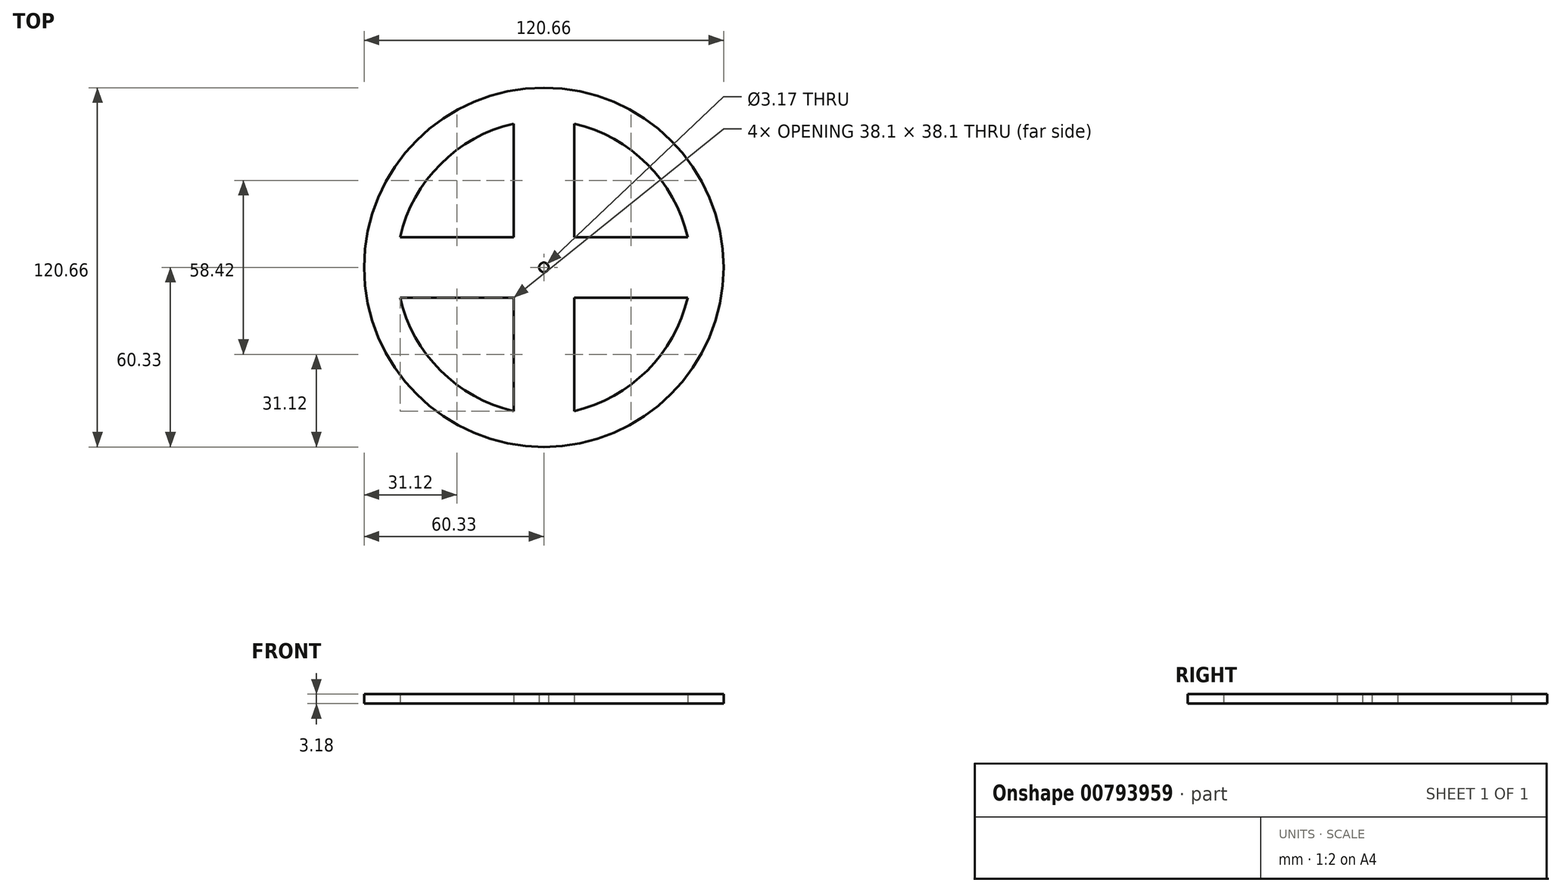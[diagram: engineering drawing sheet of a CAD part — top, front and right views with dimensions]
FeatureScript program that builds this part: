
annotation { "Feature Type Name" : "Feature", "Feature Type Description" : "" }
export const myFeature = defineFeature(function(context is Context, id is Id, definition is map)
    precondition{}
    {
        {
            var Q0;
            Q0=qCreatedBy(makeId("Top.planeOp"),FACE);
            var sketch = newSketch(context, id + "F0", { "sketchPlane" : qUnion([Q0])});
            skCircle(sketch, "E0", {"center": v(0, 0) * mm, "radius": 60.33 * mm});
            skLineSegment(sketch, "E1", {"start": v(0, 60.33) * mm, "end": v(0, 0) * mm});
            skLineSegment(sketch, "E2", {"start": v(60.33, 0) * mm, "end": v(0, 0) * mm});
            skLineSegment(sketch, "E3", {"start": v(0, -60.33) * mm, "end": v(0, 0) * mm});
            skLineSegment(sketch, "E4", {"start": v(-60.33, 0) * mm, "end": v(0, 0) * mm});
            skLineSegment(sketch, "E5", {"start": v(0, 0) * mm, "end": v(-42.66, 42.66) * mm});
            skLineSegment(sketch, "E6", {"start": v(0, 0) * mm, "end": v(42.66, 42.66) * mm});
            skLineSegment(sketch, "E7", {"start": v(0, 0) * mm, "end": v(42.66, -42.66) * mm});
            skLineSegment(sketch, "E8", {"start": v(0, 0) * mm, "end": v(-42.66, -42.66) * mm});
            skCircle(sketch, "E9", {"center": v(0, 0) * mm, "radius": 17.78 * mm});
            skLineSegment(sketch, "E10", {"start": v(0, 0) * mm, "end": v(0, 48.26) * mm});
            skLineSegment(sketch, "E11", {"start": v(0, 0) * mm, "end": v(48.26, 0) * mm});
            skLineSegment(sketch, "E12", {"start": v(0, 0) * mm, "end": v(-48.26, 0) * mm});
            skLineSegment(sketch, "E13", {"start": v(0, 0) * mm, "end": v(0, -48.26) * mm});
            skLineSegment(sketch, "E14", {"start": v(-48.26, 0) * mm, "end": v(-48.26, 10.16) * mm});
            skLineSegment(sketch, "E15", {"start": v(-48.26, 0) * mm, "end": v(-48.26, -10.16) * mm});
            skLineSegment(sketch, "E16", {"start": v(0, 48.26) * mm, "end": v(10.16, 48.26) * mm});
            skLineSegment(sketch, "E17", {"start": v(0, 48.26) * mm, "end": v(-10.16, 48.26) * mm});
            skLineSegment(sketch, "E18", {"start": v(48.26, 0) * mm, "end": v(48.26, -10.16) * mm});
            skLineSegment(sketch, "E19", {"start": v(48.26, 0) * mm, "end": v(48.26, 10.16) * mm});
            skLineSegment(sketch, "E20", {"start": v(0, -48.26) * mm, "end": v(10.16, -48.26) * mm});
            skLineSegment(sketch, "E21", {"start": v(0, -48.26) * mm, "end": v(-10.16, -48.26) * mm});
            skLineSegment(sketch, "E22.bottom", {"start": v(0, 0) * mm, "end": v(-10.16, 0) * mm});
            skLineSegment(sketch, "E22.top", {"start": v(0, 10.16) * mm, "end": v(-10.16, 10.16) * mm});
            skLineSegment(sketch, "E22.left", {"start": v(0, 0) * mm, "end": v(0, 10.16) * mm});
            skLineSegment(sketch, "E22.right", {"start": v(-10.16, 0) * mm, "end": v(-10.16, 10.16) * mm});
            skPoint(sketch, "E23.oppositeSnap0", {"position": v(-5.08, 10.16) * mm});
            skLineSegment(sketch, "E23.bottom", {"start": v(0, 0) * mm, "end": v(10.16, 0) * mm});
            skLineSegment(sketch, "E23.top", {"start": v(0, 10.16) * mm, "end": v(10.16, 10.16) * mm});
            skLineSegment(sketch, "E23.right", {"start": v(10.16, 0) * mm, "end": v(10.16, 10.16) * mm});
            skLineSegment(sketch, "E24.top", {"start": v(0, -10.16) * mm, "end": v(10.16, -10.16) * mm});
            skLineSegment(sketch, "E24.left", {"start": v(0, 0) * mm, "end": v(0, -10.16) * mm});
            skLineSegment(sketch, "E24.right", {"start": v(10.16, 0) * mm, "end": v(10.16, -10.16) * mm});
            skLineSegment(sketch, "E25.top", {"start": v(0, -10.16) * mm, "end": v(-10.16, -10.16) * mm});
            skLineSegment(sketch, "E25.right", {"start": v(-10.16, 0) * mm, "end": v(-10.16, -10.16) * mm});
            skLineSegment(sketch, "E26", {"start": v(-10.16, 48.26) * mm, "end": v(-10.16, 10.16) * mm});
            skLineSegment(sketch, "E27", {"start": v(-48.26, 10.16) * mm, "end": v(-10.16, 10.16) * mm});
            skLineSegment(sketch, "E28", {"start": v(10.16, 48.26) * mm, "end": v(10.16, 10.16) * mm});
            skLineSegment(sketch, "E29", {"start": v(48.26, 10.16) * mm, "end": v(10.16, 10.16) * mm});
            skLineSegment(sketch, "E30", {"start": v(-48.26, -10.16) * mm, "end": v(-10.16, -10.16) * mm});
            skLineSegment(sketch, "E31", {"start": v(-10.16, -10.16) * mm, "end": v(-10.16, -48.26) * mm});
            skLineSegment(sketch, "E32", {"start": v(10.16, -48.26) * mm, "end": v(10.16, -10.16) * mm});
            skLineSegment(sketch, "E33", {"start": v(48.26, -10.16) * mm, "end": v(10.16, -10.16) * mm});
            skArc(sketch, "E34", {"start": v(-10.16, 48.26) * mm, "mid": v(-34.68, 34.68) * mm, "end": v(-48.26, 10.16) * mm});
            skArc(sketch, "E35", {"start": v(48.26, 10.16) * mm, "mid": v(34.68, 34.68) * mm, "end": v(10.16, 48.26) * mm});
            skArc(sketch, "E36", {"start": v(-48.26, -10.16) * mm, "mid": v(-34.68, -34.68) * mm, "end": v(-10.16, -48.26) * mm});
            skArc(sketch, "E37", {"start": v(10.16, -48.26) * mm, "mid": v(34.68, -34.68) * mm, "end": v(48.26, -10.16) * mm});
            skCircle(sketch, "E38", {"center": v(0, 0) * mm, "radius": 1.59 * mm});
            skSolve(sketch);
        }
        {
            var Q0;
            {var subQ5=sQuery(id+"F0.wireOp",EDGE,"E16");Q0=makeQuery(id+"F0.imprint","IMPRINT",FACE,{"disambiguationData":[TD([[makeQuery(id+"F0.imprint","IMPRINT",EDGE,{"derivedFrom":subQ5}),1.0]])]});}
            var Q1;
            {var subQ0=sQuery(id+"F0.wireOp",EDGE,"E19");Q1=makeQuery(id+"F0.imprint","IMPRINT",FACE,{"disambiguationData":[TD([[makeQuery(id+"F0.imprint","IMPRINT",EDGE,{"derivedFrom":subQ0}),-1.0]])]});}
            var Q2;
            {var subQ5=sQuery(id+"F0.wireOp",EDGE,"E17");Q2=makeQuery(id+"F0.imprint","IMPRINT",FACE,{"disambiguationData":[TD([[makeQuery(id+"F0.imprint","IMPRINT",EDGE,{"derivedFrom":subQ5}),-1.0]])]});}
            var Q3;
            {var subQ5=sQuery(id+"F0.wireOp",EDGE,"E14");Q3=makeQuery(id+"F0.imprint","IMPRINT",FACE,{"disambiguationData":[TD([[makeQuery(id+"F0.imprint","IMPRINT",EDGE,{"derivedFrom":subQ5}),1.0]])]});}
            var Q4;
            {var subQ0=sQuery(id+"F0.wireOp",EDGE,"E17");Q4=makeQuery(id+"F0.imprint","IMPRINT",FACE,{"disambiguationData":[TD([[makeQuery(id+"F0.imprint","IMPRINT",EDGE,{"derivedFrom":subQ0}),1.0]])]});}
            var Q5;
            {var subQ0=sQuery(id+"F0.wireOp",EDGE,"E16");Q5=makeQuery(id+"F0.imprint","IMPRINT",FACE,{"disambiguationData":[TD([[makeQuery(id+"F0.imprint","IMPRINT",EDGE,{"derivedFrom":subQ0}),-1.0]])]});}
            var Q6;
            {var subQ0=sQuery(id+"F0.wireOp",EDGE,"E23.top");Q6=makeQuery(id+"F0.imprint","IMPRINT",FACE,{"disambiguationData":[TD([[makeQuery(id+"F0.imprint","IMPRINT",EDGE,{"derivedFrom":subQ0}),1.0]])]});}
            var Q7;
            {var subQ0=sQuery(id+"F0.wireOp",EDGE,"E22.top");Q7=makeQuery(id+"F0.imprint","IMPRINT",FACE,{"disambiguationData":[TD([[makeQuery(id+"F0.imprint","IMPRINT",EDGE,{"derivedFrom":subQ0}),-1.0]])]});}
            var Q8;
            {var subQ0=sQuery(id+"F0.wireOp",EDGE,"E22.top");Q8=makeQuery(id+"F0.imprint","IMPRINT",FACE,{"disambiguationData":[TD([[makeQuery(id+"F0.imprint","IMPRINT",EDGE,{"derivedFrom":subQ0}),1.0]])]});}
            var Q9;
            {var subQ0=sQuery(id+"F0.wireOp",EDGE,"E22.right");Q9=makeQuery(id+"F0.imprint","IMPRINT",FACE,{"disambiguationData":[TD([[makeQuery(id+"F0.imprint","IMPRINT",EDGE,{"derivedFrom":subQ0}),-1.0]])]});}
            var Q10;
            {var subQ0=sQuery(id+"F0.wireOp",EDGE,"E22.right");Q10=makeQuery(id+"F0.imprint","IMPRINT",FACE,{"disambiguationData":[TD([[makeQuery(id+"F0.imprint","IMPRINT",EDGE,{"derivedFrom":subQ0}),1.0]])]});}
            var Q11;
            {var subQ0=sQuery(id+"F0.wireOp",EDGE,"E23.right");Q11=makeQuery(id+"F0.imprint","IMPRINT",FACE,{"disambiguationData":[TD([[makeQuery(id+"F0.imprint","IMPRINT",EDGE,{"derivedFrom":subQ0}),-1.0]])]});}
            var Q12;
            {var subQ0=sQuery(id+"F0.wireOp",EDGE,"E23.top");Q12=makeQuery(id+"F0.imprint","IMPRINT",FACE,{"disambiguationData":[TD([[makeQuery(id+"F0.imprint","IMPRINT",EDGE,{"derivedFrom":subQ0}),-1.0]])]});}
            var Q13;
            {var subQ0=sQuery(id+"F0.wireOp",EDGE,"E23.right");Q13=makeQuery(id+"F0.imprint","IMPRINT",FACE,{"disambiguationData":[TD([[makeQuery(id+"F0.imprint","IMPRINT",EDGE,{"derivedFrom":subQ0}),1.0]])]});}
            var Q14;
            {var subQ0=sQuery(id+"F0.wireOp",EDGE,"E25.right");Q14=makeQuery(id+"F0.imprint","IMPRINT",FACE,{"disambiguationData":[TD([[makeQuery(id+"F0.imprint","IMPRINT",EDGE,{"derivedFrom":subQ0}),-1.0]])]});}
            var Q15;
            {var subQ0=sQuery(id+"F0.wireOp",EDGE,"E25.top");Q15=makeQuery(id+"F0.imprint","IMPRINT",FACE,{"disambiguationData":[TD([[makeQuery(id+"F0.imprint","IMPRINT",EDGE,{"derivedFrom":subQ0}),-1.0]])]});}
            var Q16;
            {var subQ0=sQuery(id+"F0.wireOp",EDGE,"E25.top");Q16=makeQuery(id+"F0.imprint","IMPRINT",FACE,{"disambiguationData":[TD([[makeQuery(id+"F0.imprint","IMPRINT",EDGE,{"derivedFrom":subQ0}),1.0]])]});}
            var Q17;
            {var subQ0=sQuery(id+"F0.wireOp",EDGE,"E24.top");Q17=makeQuery(id+"F0.imprint","IMPRINT",FACE,{"disambiguationData":[TD([[makeQuery(id+"F0.imprint","IMPRINT",EDGE,{"derivedFrom":subQ0}),-1.0]])]});}
            var Q18;
            {var subQ0=sQuery(id+"F0.wireOp",EDGE,"E24.top");Q18=makeQuery(id+"F0.imprint","IMPRINT",FACE,{"disambiguationData":[TD([[makeQuery(id+"F0.imprint","IMPRINT",EDGE,{"derivedFrom":subQ0}),1.0]])]});}
            var Q19;
            {var subQ0=sQuery(id+"F0.wireOp",EDGE,"E24.right");Q19=makeQuery(id+"F0.imprint","IMPRINT",FACE,{"disambiguationData":[TD([[makeQuery(id+"F0.imprint","IMPRINT",EDGE,{"derivedFrom":subQ0}),1.0]])]});}
            var Q20;
            {var subQ0=sQuery(id+"F0.wireOp",EDGE,"E19");Q20=makeQuery(id+"F0.imprint","IMPRINT",FACE,{"disambiguationData":[TD([[makeQuery(id+"F0.imprint","IMPRINT",EDGE,{"derivedFrom":subQ0}),1.0]])]});}
            var Q21;
            {var subQ0=sQuery(id+"F0.wireOp",EDGE,"E18");Q21=makeQuery(id+"F0.imprint","IMPRINT",FACE,{"disambiguationData":[TD([[makeQuery(id+"F0.imprint","IMPRINT",EDGE,{"derivedFrom":subQ0}),-1.0]])]});}
            var Q22;
            {var subQ0=sQuery(id+"F0.wireOp",EDGE,"E14");Q22=makeQuery(id+"F0.imprint","IMPRINT",FACE,{"disambiguationData":[TD([[makeQuery(id+"F0.imprint","IMPRINT",EDGE,{"derivedFrom":subQ0}),-1.0]])]});}
            var Q23;
            {var subQ0=sQuery(id+"F0.wireOp",EDGE,"E15");Q23=makeQuery(id+"F0.imprint","IMPRINT",FACE,{"disambiguationData":[TD([[makeQuery(id+"F0.imprint","IMPRINT",EDGE,{"derivedFrom":subQ0}),1.0]])]});}
            var Q24;
            {var subQ0=sQuery(id+"F0.wireOp",EDGE,"E21");Q24=makeQuery(id+"F0.imprint","IMPRINT",FACE,{"disambiguationData":[TD([[makeQuery(id+"F0.imprint","IMPRINT",EDGE,{"derivedFrom":subQ0}),-1.0]])]});}
            var Q25;
            {var subQ0=sQuery(id+"F0.wireOp",EDGE,"E20");Q25=makeQuery(id+"F0.imprint","IMPRINT",FACE,{"disambiguationData":[TD([[makeQuery(id+"F0.imprint","IMPRINT",EDGE,{"derivedFrom":subQ0}),1.0]])]});}
            var Q26;
            {var subQ0=sQuery(id+"F0.wireOp",EDGE,"E18");Q26=makeQuery(id+"F0.imprint","IMPRINT",FACE,{"disambiguationData":[TD([[makeQuery(id+"F0.imprint","IMPRINT",EDGE,{"derivedFrom":subQ0}),1.0]])]});}
            var Q27;
            {var subQ0=sQuery(id+"F0.wireOp",EDGE,"E20");Q27=makeQuery(id+"F0.imprint","IMPRINT",FACE,{"disambiguationData":[TD([[makeQuery(id+"F0.imprint","IMPRINT",EDGE,{"derivedFrom":subQ0}),-1.0]])]});}
            var Q28;
            {var subQ0=sQuery(id+"F0.wireOp",EDGE,"E21");Q28=makeQuery(id+"F0.imprint","IMPRINT",FACE,{"disambiguationData":[TD([[makeQuery(id+"F0.imprint","IMPRINT",EDGE,{"derivedFrom":subQ0}),1.0]])]});}
            var Q29;
            {var subQ0=sQuery(id+"F0.wireOp",EDGE,"E15");Q29=makeQuery(id+"F0.imprint","IMPRINT",FACE,{"disambiguationData":[TD([[makeQuery(id+"F0.imprint","IMPRINT",EDGE,{"derivedFrom":subQ0}),-1.0]])]});}
            var Q30;
            {var subQ0=sQuery(id+"F0.wireOp",EDGE,"E24.right");Q30=makeQuery(id+"F0.imprint","IMPRINT",FACE,{"disambiguationData":[TD([[makeQuery(id+"F0.imprint","IMPRINT",EDGE,{"derivedFrom":subQ0}),-1.0]])]});}
            var Q31;
            {var subQ0=sQuery(id+"F0.wireOp",EDGE,"E25.right");Q31=makeQuery(id+"F0.imprint","IMPRINT",FACE,{"disambiguationData":[TD([[makeQuery(id+"F0.imprint","IMPRINT",EDGE,{"derivedFrom":subQ0}),1.0]])]});}
            extrude(context, id + "F1", {"entities" : qUnion([Q0, Q1, Q2, Q3, Q4, Q5, Q6, Q7, Q8, Q9, Q10, Q11, Q12, Q13, Q14, Q15, Q16, Q17, Q18, Q19, Q20, Q21, Q22, Q23, Q24, Q25, Q26, Q27, Q28, Q29, Q30, Q31]), "depth" : 3.17 * mm, "offsetDistance" : 25.4 * mm});
        }
    });
